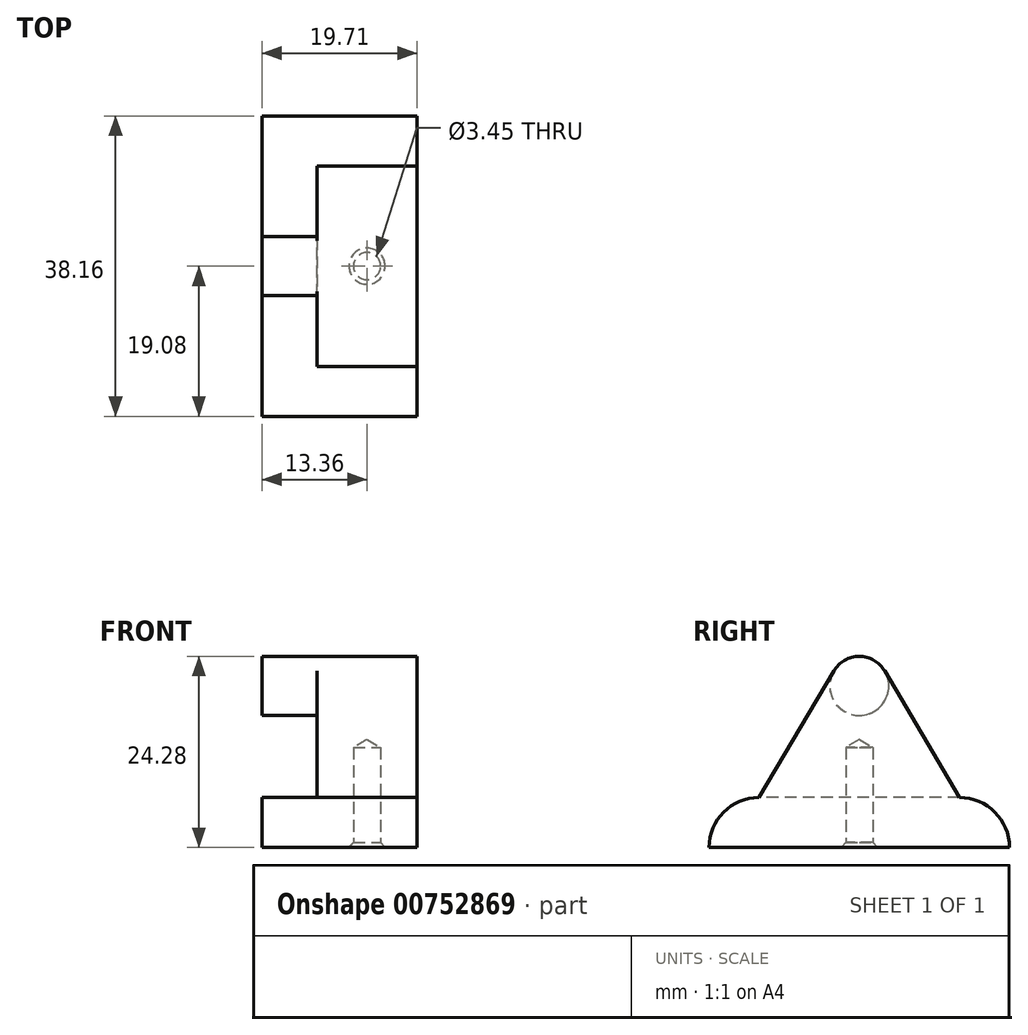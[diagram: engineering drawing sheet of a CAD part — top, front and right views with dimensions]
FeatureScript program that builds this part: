
annotation { "Feature Type Name" : "Feature", "Feature Type Description" : "" }
export const myFeature = defineFeature(function(context is Context, id is Id, definition is map)
    precondition{}
    {
        {
            var Q0;
            Q0=qCreatedBy(makeId("Right.planeOp"),FACE);
            var sketch = newSketch(context, id + "F0", { "sketchPlane" : qUnion([Q0])});
            skCircle(sketch, "E0", {"center": v(0, 0) * mm, "radius": 25 * mm});
            skCircle(sketch, "E1", {"center": v(0, 14) * mm, "radius": 11 * mm});
            skCircle(sketch, "E2", {"center": v(0, 14) * mm, "radius": 3.75 * mm});
            skLineSegment(sketch, "E3.bottom", {"start": v(12.73, -0.17) * mm, "end": v(-12.73, -0.17) * mm});
            skLineSegment(sketch, "E3.top", {"start": v(12.73, -12.87) * mm, "end": v(-12.73, -12.88) * mm});
            skLineSegment(sketch, "E3.left", {"start": v(19.08, -6.52) * mm, "end": v(19.08, -6.52) * mm});
            skLineSegment(sketch, "E3.right", {"start": v(-19.08, -6.52) * mm, "end": v(-19.08, -6.53) * mm});
            skPoint(sketch, "E3.middle", {"position": v(0, -6.52) * mm});
            skLineSegment(sketch, "E4", {"start": v(-19.08, -6.52) * mm, "end": v(19.08, -6.52) * mm});
            skPoint(sketch, "E5.visualSharp", {"position": v(-19.08, -12.88) * mm});
            skArc(sketch, "E5.filletArc", {"start": v(-19.08, -6.53) * mm, "mid": v(-17.22, -11.02) * mm, "end": v(-12.73, -12.88) * mm});
            skPoint(sketch, "E6.visualSharp", {"position": v(-19.08, -0.17) * mm});
            skArc(sketch, "E6.filletArc", {"start": v(-12.73, -0.17) * mm, "mid": v(-17.22, -2.03) * mm, "end": v(-19.08, -6.52) * mm});
            skPoint(sketch, "E7.visualSharp", {"position": v(19.08, -0.17) * mm});
            skArc(sketch, "E7.filletArc", {"start": v(19.08, -6.52) * mm, "mid": v(17.22, -2.03) * mm, "end": v(12.73, -0.17) * mm});
            skPoint(sketch, "E8.visualSharp", {"position": v(19.08, -12.87) * mm});
            skArc(sketch, "E8.filletArc", {"start": v(12.73, -12.87) * mm, "mid": v(17.22, -11.02) * mm, "end": v(19.08, -6.52) * mm});
            skLineSegment(sketch, "E9", {"start": v(-12.73, -0.17) * mm, "end": v(-3.23, 15.9) * mm});
            skLineSegment(sketch, "E10", {"start": v(12.73, -0.17) * mm, "end": v(3.23, 15.9) * mm});
            skLineSegment(sketch, "E11", {"start": v(0, -0.17) * mm, "end": v(0, -6.52) * mm});
            skLineSegment(sketch, "E12.bottom", {"start": v(-8.5, -0.17) * mm, "end": v(8.5, -0.17) * mm});
            skLineSegment(sketch, "E12.top", {"start": v(-8.5, -6.52) * mm, "end": v(8.5, -6.52) * mm});
            skLineSegment(sketch, "E12.left", {"start": v(-8.5, -0.17) * mm, "end": v(-8.5, -6.52) * mm});
            skLineSegment(sketch, "E12.right", {"start": v(8.5, -0.17) * mm, "end": v(8.5, -6.52) * mm});
            skPoint(sketch, "E12.middle", {"position": v(0, -3.35) * mm});
            skSolve(sketch);
        }
        {
            var Q0;
            Q0=makeQuery(id+"F0.imprint","IMPRINT",FACE,{"disambiguationData":[TD([[makeQuery(id+"F0.imprint","IMPRINT",EDGE,{"derivedFrom":sQuery(id+"F0.wireOp",EDGE,"E3.bottom")}),1.0]])]});
            var Q1;
            {var subQ5=sQuery(id+"F0.wireOp",EDGE,"E3.bottom");Q1=makeQuery(id+"F0.imprint","IMPRINT",FACE,{"disambiguationData":[TD([[makeQuery(id+"F0.imprint","IMPRINT",EDGE,{"derivedFrom":subQ5}),-1.0]])]});}
            var Q2;
            {var subQ0=sQuery(id+"F0.wireOp",EDGE,"E9");var subQ1=sQuery(id+"F0.wireOp",EDGE,"E1");var subQ2=makeQuery(id+"F0.imprint","INTERSECT",VERTEX,{"derivedFrom":[subQ1,subQ0]});Q2=makeQuery(id+"F0.imprint","IMPRINT",FACE,{"disambiguationData":[TD([[makeQuery(id+"F0.imprint","IMPRINT",EDGE,{"disambiguationData":[TD([[subQ2,-1.0]])],"derivedFrom":subQ1}),1.0]])]});}
            var Q3;
            {var subQ0=sQuery(id+"F0.wireOp",EDGE,"E2");var subQ1=makeQuery(id+"F0.imprint","INTERSECT",VERTEX,{"derivedFrom":[subQ0,sQuery(id+"F0.wireOp",EDGE,"E9")]});Q3=makeQuery(id+"F0.imprint","IMPRINT",FACE,{"disambiguationData":[TD([[makeQuery(id+"F0.imprint","IMPRINT",EDGE,{"disambiguationData":[TD([[subQ1,1.0]])],"derivedFrom":subQ0}),1.0]])]});}
            var Q4;
            {var subQ0=sQuery(id+"F0.wireOp",EDGE,"E11");Q4=makeQuery(id+"F0.imprint","IMPRINT",FACE,{"disambiguationData":[TD([[makeQuery(id+"F0.imprint","IMPRINT",EDGE,{"derivedFrom":subQ0}),1.0]])]});}
            var Q5;
            {var subQ0=sQuery(id+"F0.wireOp",EDGE,"E11");Q5=makeQuery(id+"F0.imprint","IMPRINT",FACE,{"disambiguationData":[TD([[makeQuery(id+"F0.imprint","IMPRINT",EDGE,{"derivedFrom":subQ0}),-1.0]])]});}
            extrude(context, id + "F1", {"entities" : qUnion([Q0, Q1, Q2, Q3, Q4, Q5]), "depth" : 12.7 * mm, "offsetDistance" : 25.4 * mm});
        }
        {
            var Q0;
            {var subQ0=sQuery(id+"F0.wireOp",EDGE,"E2");var subQ1=makeQuery(id+"F0.imprint","INTERSECT",VERTEX,{"derivedFrom":[subQ0,sQuery(id+"F0.wireOp",EDGE,"E9")]});Q0=makeQuery(id+"F0.imprint","IMPRINT",FACE,{"disambiguationData":[TD([[makeQuery(id+"F0.imprint","IMPRINT",EDGE,{"disambiguationData":[TD([[subQ1,1.0]])],"derivedFrom":subQ0}),1.0]])]});}
            extrude(context, id + "F2", {"entities" : qUnion([Q0]), "operationType" : NewBodyOperationType.ADD, "oppositeDirection" : true, "depth" : 7 * mm + 3 / 203.2 * mm, "offsetDistance" : 25.4 * mm});
        }
        {
            var Q0;
            {var subQ0=sQuery(id+"F0.wireOp",EDGE,"E7.filletArc");Q0=makeQuery(id+"F0.imprint","IMPRINT",FACE,{"disambiguationData":[TD([[makeQuery(id+"F0.imprint","IMPRINT",EDGE,{"derivedFrom":subQ0}),1.0]])]});}
            var Q1;
            {var subQ0=sQuery(id+"F0.wireOp",EDGE,"E6.filletArc");Q1=makeQuery(id+"F0.imprint","IMPRINT",FACE,{"disambiguationData":[TD([[makeQuery(id+"F0.imprint","IMPRINT",EDGE,{"derivedFrom":subQ0}),1.0]])]});}
            var Q2;
            {var subQ0=sQuery(id+"F0.wireOp",EDGE,"E11");Q2=makeQuery(id+"F0.imprint","IMPRINT",FACE,{"disambiguationData":[TD([[makeQuery(id+"F0.imprint","IMPRINT",EDGE,{"derivedFrom":subQ0}),1.0]])]});}
            var Q3;
            {var subQ0=sQuery(id+"F0.wireOp",EDGE,"E11");Q3=makeQuery(id+"F0.imprint","IMPRINT",FACE,{"disambiguationData":[TD([[makeQuery(id+"F0.imprint","IMPRINT",EDGE,{"derivedFrom":subQ0}),-1.0]])]});}
            extrude(context, id + "F3", {"entities" : qUnion([Q0, Q1, Q2, Q3]), "operationType" : NewBodyOperationType.ADD, "oppositeDirection" : true, "depth" : 7 * mm, "offsetDistance" : 25.4 * mm});
        }
        {
            var Q0;
            {var subQ0=sQuery(id+"F0.wireOp",EDGE,"E12.top");var subQ1=sQuery(id+"F0.wireOp",EDGE,"E4");Q0=makeQuery(id+"F3.boolean.opBoolean","MERGE",FACE,{"derivedFrom":[makeQuery(id+"F1.opExtrude","SWEPT_FACE",FACE,{"disambiguationData":[OSD([subQ1,subQ0])]}),makeQuery(id+"F3.opExtrude","SWEPT_FACE",FACE,{"disambiguationData":[OSD([subQ1,subQ0])]})]});}
            var sketch = newSketch(context, id + "F4", { "sketchPlane" : qUnion([Q0])});
            skLineSegment(sketch, "E13", {"start": v(0, 19.08) * mm, "end": v(0, -19.08) * mm});
            skLineSegment(sketch, "E14", {"start": v(0, 0) * mm, "end": v(12.7, 0) * mm});
            skPoint(sketch, "E15", {"position": v(6.35, 0) * mm});
            skSolve(sketch);
        }
        {
            var Q0;
            Q0=sQuery(id+"F4.wireOp",VERTEX,"E15");
            var Q1;
            Q1=makeQuery(id+"F1.opExtrude","SWEPT_BODY",BODY,{"disambiguationData":[OSD([sQuery(id+"F0.wireOp",EDGE,"E2"),sQuery(id+"F0.wireOp",EDGE,"E4"),sQuery(id+"F0.wireOp",EDGE,"E6.filletArc"),sQuery(id+"F0.wireOp",EDGE,"E7.filletArc"),sQuery(id+"F0.wireOp",EDGE,"E9"),sQuery(id+"F0.wireOp",EDGE,"E10"),sQuery(id+"F0.wireOp",EDGE,"E12.top")])]});
            hole(context, id + "F5", {"style" : HoleStyle.C_SINK, "endStyle" : HoleEndStyle.BLIND, "holeDiameter" : 3.45 * mm, "cSinkDiameter" : 4.6 * mm, "cSinkAngle" : 82 * degree, "majorDiameter" : 6.35 * mm, "holeDepth" : 12.7 * mm, "isTappedThrough" : true, "tappedDepth" : 12.7 * mm, "tapClearance" : 3, "locations" : qUnion([Q0]), "scope" : qUnion([Q1])});
        }
    });
